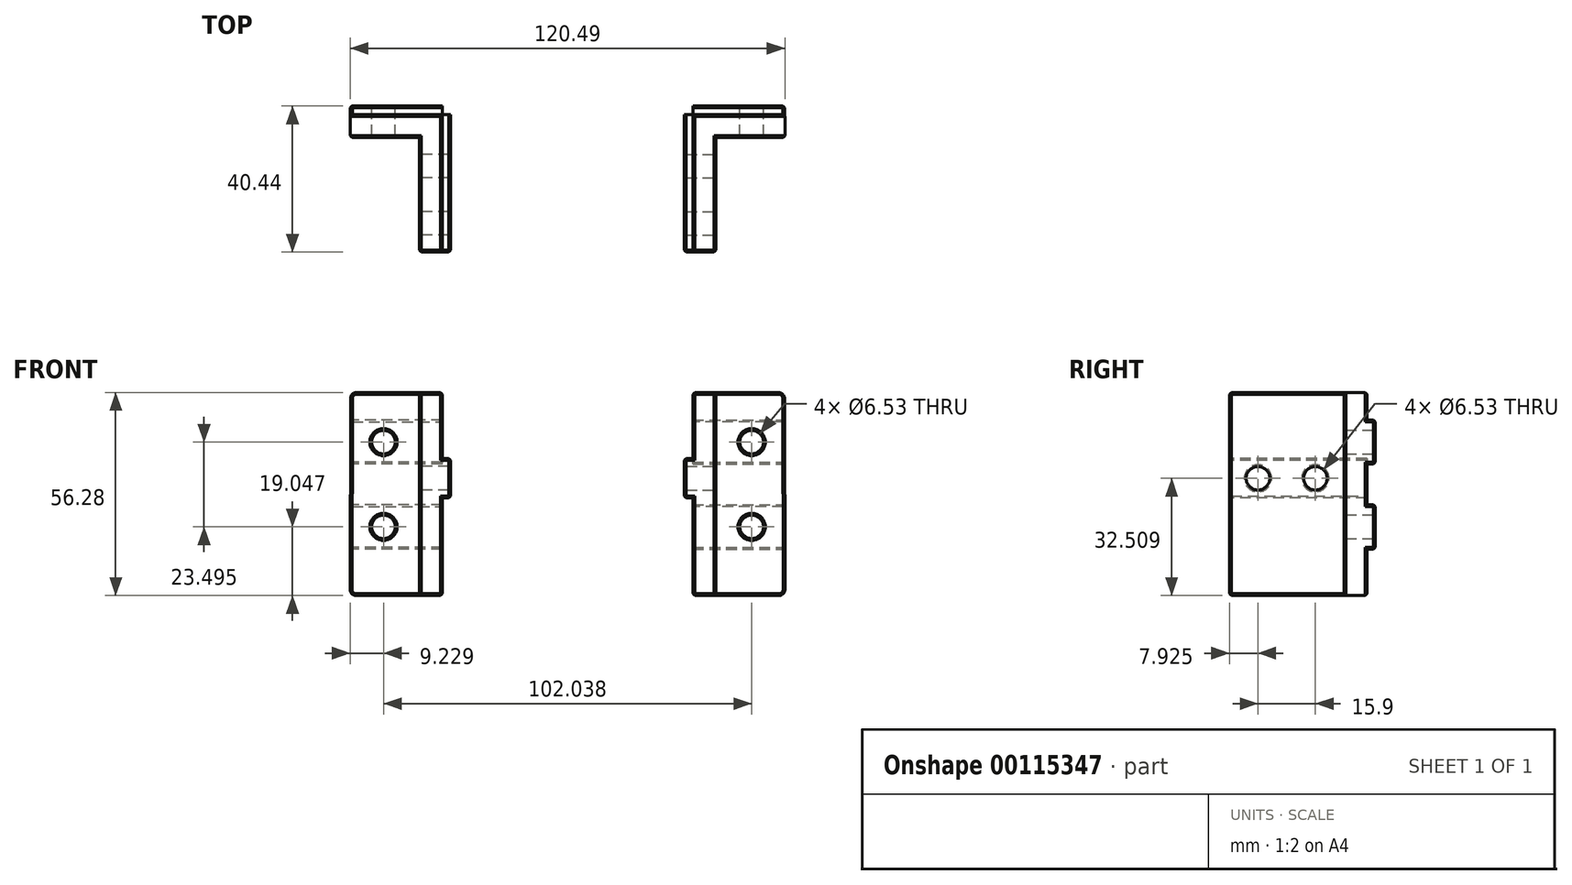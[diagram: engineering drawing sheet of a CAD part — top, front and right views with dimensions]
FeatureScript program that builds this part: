
annotation { "Feature Type Name" : "Feature", "Feature Type Description" : "" }
export const myFeature = defineFeature(function(context is Context, id is Id, definition is map)
    precondition{}
    {
        {
            var Q0;
            Q0=qCreatedBy(makeId("Front.planeOp"),FACE);
            var sketch = newSketch(context, id + "F0", { "sketchPlane" : qUnion([Q0])});
            skLineSegment(sketch, "E0.right", {"start": v(-57.15, -28.14) * mm, "end": v(-57.05, 28.14) * mm});
            skCircle(sketch, "E1", {"center": v(-47.92, -9.1) * mm, "radius": 3.26 * mm});
            skCircle(sketch, "E2", {"center": v(-47.92, 14.4) * mm, "radius": 3.26 * mm});
            skLineSegment(sketch, "E3.bottom", {"start": v(-38, 28.14) * mm, "end": v(-31.65, 28.14) * mm});
            skLineSegment(sketch, "E3.top", {"start": v(-38, -28.14) * mm, "end": v(-31.65, -28.14) * mm});
            skLineSegment(sketch, "E3.left", {"start": v(-38, 28.14) * mm, "end": v(-38, -28.14) * mm});
            skLineSegment(sketch, "E3.right", {"start": v(-31.65, 28.14) * mm, "end": v(-31.65, -28.14) * mm});
            skLineSegment(sketch, "E4.trimOffspring", {"start": v(-31.65, 28.14) * mm, "end": v(-57.05, 28.14) * mm});
            skLineSegment(sketch, "E5.trimOffspring", {"start": v(-31.65, -28.14) * mm, "end": v(-57.15, -28.14) * mm});
            skSolve(sketch);
        }
        {
            var Q0;
            {var subQ0=sQuery(id+"F0.wireOp",EDGE,"E3.left");Q0=makeQuery(id+"F0.imprint","IMPRINT",FACE,{"disambiguationData":[TD([[makeQuery(id+"F0.imprint","IMPRINT",EDGE,{"derivedFrom":subQ0}),1.0]])]});}
            var Q1;
            {var subQ0=sQuery(id+"F0.wireOp",EDGE,"11c7a131-536c-42c2-9c47-560869c349ee9.MirrorCS");Q1=makeQuery(id+"F0.imprint","IMPRINT",FACE,{"disambiguationData":[TD([[makeQuery(id+"F0.imprint","IMPRINT",EDGE,{"derivedFrom":subQ0}),1.0]])]});}
            extrude(context, id + "F1", {"entities" : qUnion([Q0, Q1]), "depth" : 38.1 * mm});
        }
        {
            var Q0;
            {var subQ0=sQuery(id+"F0.wireOp",EDGE,"E0.right");Q0=makeQuery(id+"F0.imprint","IMPRINT",FACE,{"disambiguationData":[TD([[makeQuery(id+"F0.imprint","IMPRINT",EDGE,{"derivedFrom":subQ0}),-1.0]])]});}
            var Q1;
            Q1=makeQuery(id+"F0.imprint","IMPRINT",FACE,{"disambiguationData":[TD([[makeQuery(id+"F0.imprint","IMPRINT",EDGE,{"derivedFrom":sQuery(id+"F0.wireOp",EDGE,"11c7a131-536c-42c2-9c47-560869c349ee2.MirrorC")}),1.0]])]});
            extrude(context, id + "F2", {"entities" : qUnion([Q0, Q1]), "depth" : 6.35 * mm});
        }
        {
            var Q0;
            Q0=makeQuery(id+"F1.opExtrude","SWEPT_BODY",BODY,{"disambiguationData":[OSD([sQuery(id+"F0.wireOp",EDGE,"11c7a131-536c-42c2-9c47-560869c349ee9.MirrorCS"),sQuery(id+"F0.wireOp",EDGE,"11c7a131-536c-42c2-9c47-560869c349ee10.MirrorCS"),sQuery(id+"F0.wireOp",EDGE,"11c7a131-536c-42c2-9c47-560869c349ee13.MirrorCS"),sQuery(id+"F0.wireOp",EDGE,"11c7a131-536c-42c2-9c47-560869c349ee14.MirrorCS")])]});
            var Q1;
            Q1=makeQuery(id+"F2.opExtrude","SWEPT_BODY",BODY,{"disambiguationData":[OSD([sQuery(id+"F0.wireOp",EDGE,"E0.right"),sQuery(id+"F0.wireOp",EDGE,"QpIMxTwa-ffh6-dxYi-KdPb-LVVgsQsY0O9s"),sQuery(id+"F0.wireOp",EDGE,"P3sMfWQC-Z2pu-dSH3-uiyq-jJdyyCvwo2wO"),sQuery(id+"F0.wireOp",EDGE,"E1"),sQuery(id+"F0.wireOp",EDGE,"E2"),sQuery(id+"F0.wireOp",EDGE,"E3.left"),sQuery(id+"F0.wireOp",EDGE,"E4.trimOffspring"),sQuery(id+"F0.wireOp",EDGE,"E5.trimOffspring")])]});
            var Q2;
            Q2=makeQuery(id+"F1.opExtrude","SWEPT_BODY",BODY,{"disambiguationData":[OSD([sQuery(id+"F0.wireOp",EDGE,"E3.left"),sQuery(id+"F0.wireOp",EDGE,"E4.trimOffspring"),sQuery(id+"F0.wireOp",EDGE,"E5.trimOffspring"),sQuery(id+"F0.wireOp",EDGE,"E3.right")])]});
            var Q3;
            Q3=makeQuery(id+"F2.opExtrude","SWEPT_BODY",BODY,{"disambiguationData":[OSD([sQuery(id+"F0.wireOp",EDGE,"fExpi3Y8-JXBf-TWYs-A3Gx-c4xyJE7IG7cL"),sQuery(id+"F0.wireOp",EDGE,"d8bed7d8-23bc-4bae-bc93-c6f59c7507a6"),sQuery(id+"F0.wireOp",EDGE,"sJCnFxoI-7eCt-0gWt-7qQj-VGD27GjXpaHk.bottom"),sQuery(id+"F0.wireOp",EDGE,"sJCnFxoI-7eCt-0gWt-7qQj-VGD27GjXpaHk.top"),sQuery(id+"F0.wireOp",EDGE,"E3.right"),sQuery(id+"F0.wireOp",EDGE,"11c7a131-536c-42c2-9c47-560869c349ee5.MirrorC"),sQuery(id+"F0.wireOp",EDGE,"11c7a131-536c-42c2-9c47-560869c349ee8.MirrorC"),sQuery(id+"F0.wireOp",EDGE,"11c7a131-536c-42c2-9c47-560869c349ee9.MirrorCS"),sQuery(id+"F0.wireOp",EDGE,"11c7a131-536c-42c2-9c47-560869c349ee11.MirrorCS"),sQuery(id+"F0.wireOp",EDGE,"11c7a131-536c-42c2-9c47-560869c349ee12.MirrorCS")])]});
            var Q4;
            Q4=makeQuery(id+"F2.opExtrude","SWEPT_BODY",BODY,{"disambiguationData":[OSD([sQuery(id+"F0.wireOp",EDGE,"11c7a131-536c-42c2-9c47-560869c349ee2.MirrorC"),sQuery(id+"F0.wireOp",EDGE,"11c7a131-536c-42c2-9c47-560869c349ee3.MirrorC"),sQuery(id+"F0.wireOp",EDGE,"11c7a131-536c-42c2-9c47-560869c349ee4.MirrorC"),sQuery(id+"F0.wireOp",EDGE,"11c7a131-536c-42c2-9c47-560869c349ee6.MirrorC"),sQuery(id+"F0.wireOp",EDGE,"11c7a131-536c-42c2-9c47-560869c349ee10.MirrorCS"),sQuery(id+"F0.wireOp",EDGE,"11c7a131-536c-42c2-9c47-560869c349ee13.MirrorCS"),sQuery(id+"F0.wireOp",EDGE,"11c7a131-536c-42c2-9c47-560869c349ee14.MirrorCS"),sQuery(id+"F0.wireOp",EDGE,"11c7a131-536c-42c2-9c47-560869c349ee15.MirrorCS")])]});
            booleanBodies(context, id + "F3", {"operationType" : BooleanOperationType.UNION, "tools" : qUnion([Q0, Q1, Q2, Q3, Q4])});
        }
        {
            var Q0;
            Q0=makeQuery(id+"F2.opExtrude","SWEPT_EDGE",EDGE,{"disambiguationData":[OSD([sQuery(id+"F0.wireOp",EDGE,"11c7a131-536c-42c2-9c47-560869c349ee13.MirrorCS"),sQuery(id+"F0.wireOp",EDGE,"11c7a131-536c-42c2-9c47-560869c349ee15.MirrorCS")])]});
            var Q1;
            Q1=makeQuery(id+"F2.opExtrude","SWEPT_EDGE",EDGE,{"disambiguationData":[OSD([sQuery(id+"F0.wireOp",EDGE,"E0.right"),sQuery(id+"F0.wireOp",EDGE,"E4.trimOffspring")])]});
            var Q2;
            Q2=makeQuery(id+"F2.opExtrude","SWEPT_EDGE",EDGE,{"disambiguationData":[OSD([sQuery(id+"F0.wireOp",EDGE,"11c7a131-536c-42c2-9c47-560869c349ee14.MirrorCS"),sQuery(id+"F0.wireOp",EDGE,"11c7a131-536c-42c2-9c47-560869c349ee15.MirrorCS")])]});
            var Q3;
            Q3=makeQuery(id+"F2.opExtrude","SWEPT_EDGE",EDGE,{"disambiguationData":[OSD([sQuery(id+"F0.wireOp",EDGE,"E0.right"),sQuery(id+"F0.wireOp",EDGE,"E5.trimOffspring")])]});
            var Q4;
            Q4=makeQuery(id+"F1.opExtrude","CAP_EDGE",EDGE,{"disambiguationData":[OSD([sQuery(id+"F0.wireOp",EDGE,"E4.trimOffspring")])],"isStart":false});
            var Q5;
            Q5=makeQuery(id+"F1.opExtrude","CAP_EDGE",EDGE,{"disambiguationData":[OSD([sQuery(id+"F0.wireOp",EDGE,"E5.trimOffspring")])],"isStart":false});
            var Q6;
            Q6=makeQuery(id+"F1.opExtrude","CAP_EDGE",EDGE,{"disambiguationData":[OSD([sQuery(id+"F0.wireOp",EDGE,"11c7a131-536c-42c2-9c47-560869c349ee13.MirrorCS")])],"isStart":false});
            var Q7;
            Q7=makeQuery(id+"F1.opExtrude","CAP_EDGE",EDGE,{"disambiguationData":[OSD([sQuery(id+"F0.wireOp",EDGE,"11c7a131-536c-42c2-9c47-560869c349ee14.MirrorCS")])],"isStart":false});
            fillet(context, id + "F4", {"entities" : qUnion([Q0, Q1, Q2, Q3, Q4, Q5, Q6, Q7]), "radius" : 1.6 * mm, "tangentPropagation" : true, "allowEdgeOverflow" : false});
        }
        {
            var Q0;
            {var subQ0=sQuery(id+"F0.wireOp",EDGE,"E5.trimOffspring");var subQ1=sQuery(id+"F0.wireOp",EDGE,"E4.trimOffspring");var subQ2=sQuery(id+"F0.wireOp",EDGE,"E3.left");Q0=makeQuery(id+"F3.opBoolean","MERGE",FACE,{"derivedFrom":[makeQuery(id+"F1.opExtrude","CAP_FACE",FACE,{"disambiguationData":[OSD([subQ2,subQ1,subQ0,sQuery(id+"F0.wireOp",EDGE,"E3.right")])],"isStart":true}),makeQuery(id+"F2.opExtrude","CAP_FACE",FACE,{"disambiguationData":[OSD([sQuery(id+"F0.wireOp",EDGE,"E0.right"),sQuery(id+"F0.wireOp",EDGE,"E1"),sQuery(id+"F0.wireOp",EDGE,"E2"),subQ2,subQ1,subQ0])],"isStart":true})]});}
            var sketch = newSketch(context, id + "F5", { "sketchPlane" : qUnion([Q0])});
            skLineSegment(sketch, "E6.bottom", {"start": v(31.65, 20.54) * mm, "end": v(57.06, 20.54) * mm});
            skLineSegment(sketch, "E6.top", {"start": v(31.65, 8.27) * mm, "end": v(57.09, 8.27) * mm});
            skLineSegment(sketch, "E6.left", {"start": v(31.65, 20.54) * mm, "end": v(31.65, 8.27) * mm});
            skPoint(sketch, "E6.middle", {"position": v(47.92, 14.4) * mm});
            skLineSegment(sketch, "E7.bottom", {"start": v(31.65, -2.97) * mm, "end": v(57.1, -2.97) * mm});
            skLineSegment(sketch, "E7.top", {"start": v(31.65, -15.24) * mm, "end": v(57.13, -15.24) * mm});
            skLineSegment(sketch, "E7.left", {"start": v(31.65, -2.97) * mm, "end": v(31.65, -15.24) * mm});
            skPoint(sketch, "E7.middle", {"position": v(47.92, -9.1) * mm});
            skLineSegment(sketch, "E8", {"start": v(57.06, 20.54) * mm, "end": v(57.09, 8.27) * mm});
            skLineSegment(sketch, "E9", {"start": v(57.1, -2.97) * mm, "end": v(57.13, -15.24) * mm});
            skSolve(sketch);
        }
        {
            var Q0;
            Q0=makeQuery(id+"F5.imprint","IMPRINT",FACE,{"disambiguationData":[TD([[makeQuery(id+"F5.imprint","IMPRINT",EDGE,{"derivedFrom":sQuery(id+"F5.wireOp",EDGE,"E6.bottom")}),-1.0]])]});
            var Q1;
            Q1=makeQuery(id+"F5.imprint","IMPRINT",FACE,{"disambiguationData":[TD([[makeQuery(id+"F5.imprint","IMPRINT",EDGE,{"derivedFrom":sQuery(id+"F5.wireOp",EDGE,"E7.bottom")}),-1.0]])]});
            extrude(context, id + "F6", {"entities" : qUnion([Q0, Q1]), "operationType" : NewBodyOperationType.ADD, "depth" : 2.34 * mm});
        }
        {
            var Q0;
            Q0=makeQuery(id+"F1.opExtrude","SWEPT_FACE",FACE,{"disambiguationData":[OSD([sQuery(id+"F0.wireOp",EDGE,"E3.left")])]});
            var sketch = newSketch(context, id + "F7", { "sketchPlane" : qUnion([Q0])});
            skCircle(sketch, "E10", {"center": v(14.27, 4.37) * mm, "radius": 3.26 * mm});
            skCircle(sketch, "E11", {"center": v(30.18, 4.37) * mm, "radius": 3.26 * mm});
            skLineSegment(sketch, "E12.top", {"start": v(38.1, 9.8) * mm, "end": v(0, 9.8) * mm});
            skLineSegment(sketch, "E13.MirrorCS", {"start": v(38.1, -1.04) * mm, "end": v(0, -1.04) * mm});
            skLineSegment(sketch, "E14", {"start": v(38.1, 9.8) * mm, "end": v(38.1, -1.04) * mm});
            skLineSegment(sketch, "E15", {"start": v(0, 9.8) * mm, "end": v(0, -1.04) * mm});
            skSolve(sketch);
        }
        {
            var Q0;
            Q0=makeQuery(id+"F7.imprint","IMPRINT",FACE,{"disambiguationData":[TD([[makeQuery(id+"F7.imprint","IMPRINT",EDGE,{"derivedFrom":sQuery(id+"F7.wireOp",EDGE,"E11")}),1.0]])]});
            var Q1;
            Q1=makeQuery(id+"F7.imprint","IMPRINT",FACE,{"disambiguationData":[TD([[makeQuery(id+"F7.imprint","IMPRINT",EDGE,{"derivedFrom":sQuery(id+"F7.wireOp",EDGE,"E10")}),1.0]])]});
            extrude(context, id + "F8", {"entities" : qUnion([Q0, Q1]), "operationType" : NewBodyOperationType.REMOVE, "oppositeDirection" : true, "depth" : 25.4 * mm});
        }
        {
            var Q0;
            Q0=qSketchRegion(id+"F7",true);
            extrude(context, id + "F9", {"entities" : qUnion([Q0]), "operationType" : NewBodyOperationType.ADD, "oppositeDirection" : true, "depth" : 8.71 * mm});
        }
        {
            var Q0;
            {var subQ0=sQuery(id+"F0.wireOp",EDGE,"E4.trimOffspring");Q0=makeQuery(id+"F3.opBoolean","MERGE",FACE,{"derivedFrom":[makeQuery(id+"F1.opExtrude","SWEPT_FACE",FACE,{"disambiguationData":[OSD([subQ0])]}),makeQuery(id+"F2.opExtrude","SWEPT_FACE",FACE,{"disambiguationData":[OSD([subQ0])]})]});}
            var Q1;
            Q1=makeQuery(id+"F9.boolean.opBoolean","MERGE",FACE,{"derivedFrom":[makeQuery(id+"F1.opExtrude","CAP_FACE",FACE,{"disambiguationData":[OSD([sQuery(id+"F0.wireOp",EDGE,"E3.left"),sQuery(id+"F0.wireOp",EDGE,"E4.trimOffspring"),sQuery(id+"F0.wireOp",EDGE,"E5.trimOffspring"),sQuery(id+"F0.wireOp",EDGE,"E3.right")])],"isStart":false}),makeQuery(id+"F9.opExtrude","SWEPT_FACE",FACE,{"disambiguationData":[OSD([sQuery(id+"F7.wireOp",EDGE,"E14")])]})]});
            var Q2;
            {var subQ0=sQuery(id+"F0.wireOp",EDGE,"E5.trimOffspring");Q2=makeQuery(id+"F3.opBoolean","MERGE",FACE,{"derivedFrom":[makeQuery(id+"F1.opExtrude","SWEPT_FACE",FACE,{"disambiguationData":[OSD([subQ0])]}),makeQuery(id+"F2.opExtrude","SWEPT_FACE",FACE,{"disambiguationData":[OSD([subQ0])]})]});}
            var Q3;
            Q3=makeQuery(id+"F6.opExtrude","CAP_EDGE",EDGE,{"disambiguationData":[OSD([sQuery(id+"F0.wireOp",EDGE,"E1")])],"isStart":false});
            var Q4;
            Q4=makeQuery(id+"F6.opExtrude","CAP_EDGE",EDGE,{"disambiguationData":[OSD([sQuery(id+"F0.wireOp",EDGE,"E2")])],"isStart":false});
            var Q5;
            Q5=makeQuery(id+"F9.opExtrude","CAP_EDGE",EDGE,{"disambiguationData":[OSD([sQuery(id+"F7.wireOp",EDGE,"E10")])],"isStart":false});
            var Q6;
            Q6=makeQuery(id+"F9.opExtrude","CAP_EDGE",EDGE,{"disambiguationData":[OSD([sQuery(id+"F7.wireOp",EDGE,"E11")])],"isStart":false});
            var Q7;
            Q7=makeQuery(id+"F8.boolean.opBoolean","COPY",EDGE,{"derivedFrom":makeQuery(id+"F8.opExtrude","CAP_EDGE",EDGE,{"disambiguationData":[OSD([sQuery(id+"F7.wireOp",EDGE,"E10")])],"isStart":true})});
            var Q8;
            Q8=makeQuery(id+"F8.boolean.opBoolean","COPY",EDGE,{"derivedFrom":makeQuery(id+"F8.opExtrude","CAP_EDGE",EDGE,{"disambiguationData":[OSD([sQuery(id+"F7.wireOp",EDGE,"E11")])],"isStart":true})});
            var Q9;
            Q9=makeQuery(id+"F2.opExtrude","CAP_EDGE",EDGE,{"disambiguationData":[OSD([sQuery(id+"F0.wireOp",EDGE,"E2")])],"isStart":false});
            var Q10;
            Q10=makeQuery(id+"F2.opExtrude","CAP_EDGE",EDGE,{"disambiguationData":[OSD([sQuery(id+"F0.wireOp",EDGE,"E1")])],"isStart":false});
            var Q11;
            Q11=makeQuery(id+"F6.boolean.opBoolean","MERGE",FACE,{"derivedFrom":[makeQuery(id+"F2.opExtrude","SWEPT_FACE",FACE,{"disambiguationData":[OSD([sQuery(id+"F0.wireOp",EDGE,"E0.right")])]}),makeQuery(id+"F6.opExtrude","SWEPT_FACE",FACE,{"disambiguationData":[OSD([sQuery(id+"F5.wireOp",EDGE,"E8")])]}),makeQuery(id+"F6.opExtrude","SWEPT_FACE",FACE,{"disambiguationData":[OSD([sQuery(id+"F5.wireOp",EDGE,"E9")])]})]});
            var Q12;
            Q12=makeQuery(id+"F6.opExtrude","CAP_EDGE",EDGE,{"disambiguationData":[OSD([sQuery(id+"F5.wireOp",EDGE,"E7.top")])],"isStart":false});
            var Q13;
            Q13=makeQuery(id+"F6.opExtrude","CAP_EDGE",EDGE,{"disambiguationData":[OSD([sQuery(id+"F5.wireOp",EDGE,"E7.bottom")])],"isStart":false});
            var Q14;
            Q14=makeQuery(id+"F6.opExtrude","CAP_EDGE",EDGE,{"disambiguationData":[OSD([sQuery(id+"F5.wireOp",EDGE,"E6.top")])],"isStart":false});
            var Q15;
            Q15=makeQuery(id+"F6.opExtrude","CAP_EDGE",EDGE,{"disambiguationData":[OSD([sQuery(id+"F5.wireOp",EDGE,"E6.bottom")])],"isStart":false});
            var Q16;
            Q16=makeQuery(id+"F9.opExtrude","CAP_EDGE",EDGE,{"disambiguationData":[OSD([sQuery(id+"F7.wireOp",EDGE,"E13.MirrorCS")])],"isStart":false});
            var Q17;
            Q17=makeQuery(id+"F9.opExtrude","CAP_EDGE",EDGE,{"disambiguationData":[OSD([sQuery(id+"F7.wireOp",EDGE,"E12.top")])],"isStart":false});
            chamfer(context, id + "F10", {"entities" : qUnion([Q0, Q1, Q2, Q3, Q4, Q5, Q6, Q7, Q8, Q9, Q10, Q11, Q12, Q13, Q14, Q15, Q16, Q17]), "width" : 0.5 * mm, "tangentPropagation" : true});
        }
        {
            var Q0;
            Q0=makeQuery(id+"F9.opExtrude","CAP_FACE",FACE,{"disambiguationData":[OSD([sQuery(id+"F7.wireOp",EDGE,"E10"),sQuery(id+"F7.wireOp",EDGE,"E11"),sQuery(id+"F7.wireOp",EDGE,"E12.top"),sQuery(id+"F7.wireOp",EDGE,"E13.MirrorCS"),sQuery(id+"F7.wireOp",EDGE,"E14"),sQuery(id+"F7.wireOp",EDGE,"E15")])],"isStart":false});
            cPlane(context, id + "F11", {"entities" : qUnion([Q0]), "cplaneType" : CPlaneType.OFFSET, "offset" : 32.38 * mm, "width" : 152.4 * mm, "height" : 152.4 * mm});
        }
        {
            var Q0;
            Q0=makeQuery(id+"F2.opExtrude","SWEPT_BODY",BODY,{"disambiguationData":[OSD([sQuery(id+"F0.wireOp",EDGE,"E0.right"),sQuery(id+"F0.wireOp",EDGE,"E1"),sQuery(id+"F0.wireOp",EDGE,"E2"),sQuery(id+"F0.wireOp",EDGE,"E3.left"),sQuery(id+"F0.wireOp",EDGE,"E4.trimOffspring"),sQuery(id+"F0.wireOp",EDGE,"E5.trimOffspring")])]});
            var Q1;
            Q1=qCreatedBy(id+"F11.planeOp",FACE);
            mirror(context, id + "F12", {"entities" : qUnion([Q0]), "mirrorPlane" : qUnion([Q1])});
        }
        {
            var Q0;
            Q0=makeQuery(id+"F2.opExtrude","SWEPT_BODY",BODY,{"disambiguationData":[OSD([sQuery(id+"F0.wireOp",EDGE,"E0.right"),sQuery(id+"F0.wireOp",EDGE,"E1"),sQuery(id+"F0.wireOp",EDGE,"E2"),sQuery(id+"F0.wireOp",EDGE,"E3.left"),sQuery(id+"F0.wireOp",EDGE,"E4.trimOffspring"),sQuery(id+"F0.wireOp",EDGE,"E5.trimOffspring")])]});
            deleteBodies(context, id + "F13", {"entities" : qUnion([Q0])});
        }
        {
            var Q0;
            Q0=makeQuery(id+"F12.opPattern","COPY",BODY,{"derivedFrom":makeQuery(id+"F2.opExtrude","SWEPT_BODY",BODY,{"disambiguationData":[OSD([sQuery(id+"F0.wireOp",EDGE,"E0.right"),sQuery(id+"F0.wireOp",EDGE,"E1"),sQuery(id+"F0.wireOp",EDGE,"E2"),sQuery(id+"F0.wireOp",EDGE,"E3.left"),sQuery(id+"F0.wireOp",EDGE,"E4.trimOffspring"),sQuery(id+"F0.wireOp",EDGE,"E5.trimOffspring")])]}),"instanceName":"1"});
            var Q1;
            Q1=qCreatedBy(id+"F11.planeOp",FACE);
            mirror(context, id + "F14", {"entities" : qUnion([Q0]), "mirrorPlane" : qUnion([Q1])});
        }
    });
